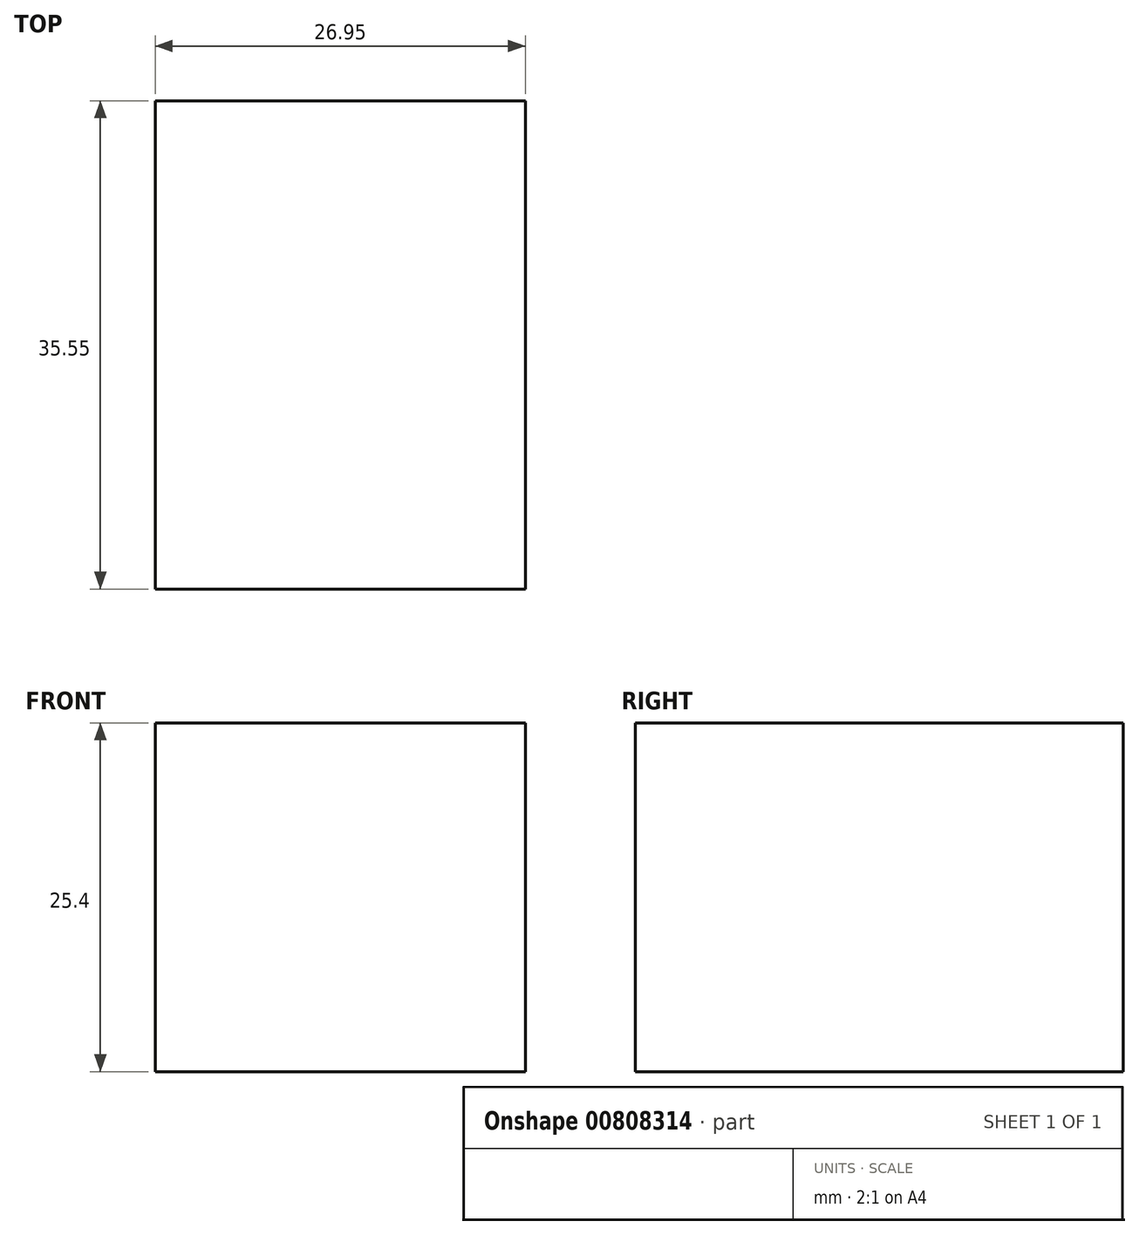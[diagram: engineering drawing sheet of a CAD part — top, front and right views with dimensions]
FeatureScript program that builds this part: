
annotation { "Feature Type Name" : "Feature", "Feature Type Description" : "" }
export const myFeature = defineFeature(function(context is Context, id is Id, definition is map)
    precondition{}
    {
        {
            var Q0;
            Q0=qCreatedBy(makeId("Top.planeOp"),FACE);
            var sketch = newSketch(context, id + "F0", { "sketchPlane" : qUnion([Q0])});
            skLineSegment(sketch, "E0.bottom", {"start": v(0, 0) * mm, "end": v(-26.95, 0) * mm});
            skLineSegment(sketch, "E0.top", {"start": v(0, 35.55) * mm, "end": v(-26.95, 35.55) * mm});
            skLineSegment(sketch, "E0.left", {"start": v(0, 0) * mm, "end": v(0, 35.55) * mm});
            skLineSegment(sketch, "E0.right", {"start": v(-26.95, 0) * mm, "end": v(-26.95, 35.55) * mm});
            skSolve(sketch);
        }
        {
            var Q0;
            Q0 = qSketchRegion(id + "F0", true);
            extrude(context, id + "F1", {"entities" : qUnion([Q0]), "depth" : 25.4 * mm, "offsetDistance" : 25.4 * mm});
        }
    });
